# Revit family: Specialty_Door-Acudor-Flush-ACF-2064_Series
name_source: partatom
category: Specialty Equipment
revit_build: Autodesk Revit 2014 (Build: 20130308_1515(x64)
units: mm (PartAtom-declared; Revit-internal decimal feet)

## types (4) — shared parameters
Assembly Code = C1020700
Default Elevation = 48"
Description = Steel Flush Acoustical Access Door
Finish = Steel-Acudor-18 GA-White Baked-On Enamel
Installation Type = Wall Mounted
Length = 2 25/32"
Manufacturer = Acudor
Material = Steel-Acudor-18 GA-White Baked-On Enamel
Product Documentation Link = https://www.acudor.com
Product Page URL = https://www.acudor.com
Screwdriver Operated Compression Latch = Yes
URL = http://acudor.com

## per-type parameters (varying)
| type | 1 Latch | 2 Latch | Height | Width |
| ACF-2064 12x12 | Yes | No | 12" | 12" |
| ACF-2064 18x18 | Yes | No | 18" | 18" |
| ACF-2064 24x24 | Yes | No | 24" | 24" |
| ACF-2064 24x36 | No | Yes | 36" | 24" |

note: column(s) folded — value = type name in every type: Model

## geometry (parser evidence)
native form markers: Sweep x1
no freeform markers — native parametric forms only
